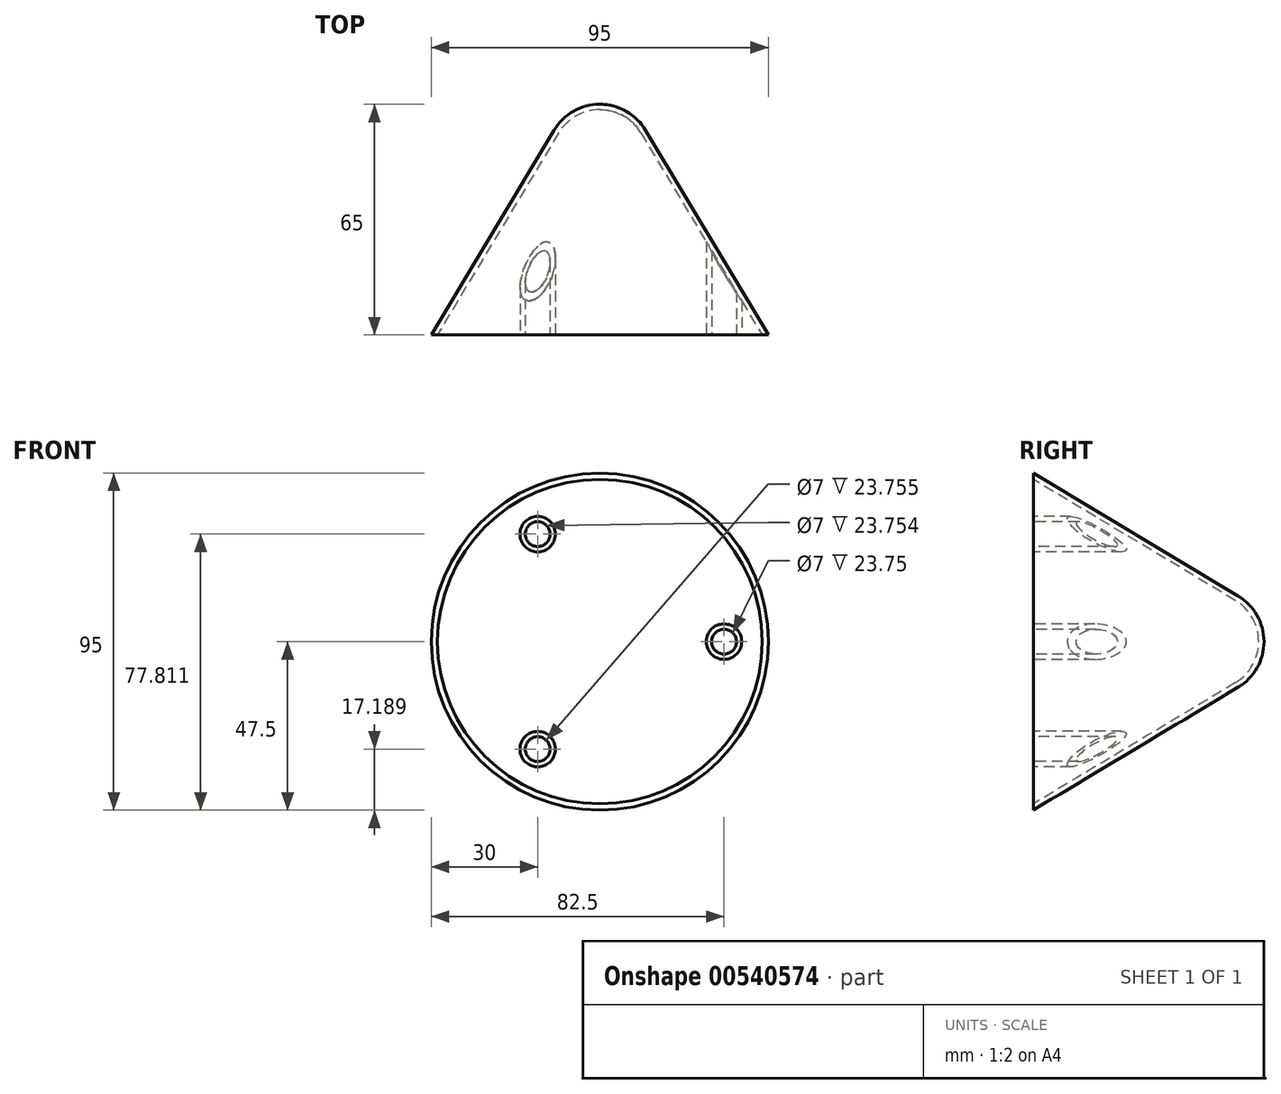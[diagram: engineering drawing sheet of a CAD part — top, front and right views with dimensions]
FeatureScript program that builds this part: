
annotation { "Feature Type Name" : "Feature", "Feature Type Description" : "" }
export const myFeature = defineFeature(function(context is Context, id is Id, definition is map)
    precondition{}
    {
        {
            var Q0;
            Q0=qCreatedBy(makeId("Top.planeOp"),FACE);
            var sketch = newSketch(context, id + "F0", { "sketchPlane" : qUnion([Q0])});
            skLineSegment(sketch, "E0", {"start": v(0, 0) * mm, "end": v(47.5, 0) * mm});
            skLineSegment(sketch, "E1", {"start": v(0, 0) * mm, "end": v(0, 50) * mm});
            skArc(sketch, "E2", {"start": v(12.86, 57.72) * mm, "mid": v(7.39, 63.05) * mm, "end": v(0, 65) * mm});
            skLineSegment(sketch, "E3", {"start": v(12.86, 57.72) * mm, "end": v(47.5, 0) * mm});
            skLineSegment(sketch, "E4", {"start": v(0, 50) * mm, "end": v(0, 77.84) * mm});
            skPoint(sketch, "E5.orphan", {"position": v(-12.86, 57.72) * mm});
            skSolve(sketch);
        }
        {
            var Q0;
            Q0=makeQuery(id+"F0.imprint","IMPRINT",FACE,{"disambiguationData":[TD([[makeQuery(id+"F0.imprint","IMPRINT",EDGE,{"derivedFrom":sQuery(id+"F0.wireOp",EDGE,"E0")}),1.0]])]});
            var Q1;
            Q1=sQuery(id+"F0.wireOp",EDGE,"E1");
            revolve(context, id + "F1", {"entities" : qUnion([Q0]), "axis" : qUnion([Q1]), "revolveType" : RevolveType.FULL});
        }
        {
            var Q0;
            Q0=makeQuery(id+"F1.opRevolve","SWEPT_FACE",FACE,{"disambiguationData":[OSD([sQuery(id+"F0.wireOp",EDGE,"E0")])]});
            shell(context, id + "F2", {"entities" : qUnion([Q0]), "thickness" : 1.5 * mm});
        }
        {
            var Q0;
            Q0=qCreatedBy(makeId("Front.planeOp"),FACE);
            var sketch = newSketch(context, id + "F3", { "sketchPlane" : qUnion([Q0])});
            skCircle(sketch, "E6", {"center": v(35, 0) * mm, "radius": 5 * mm});
            skCircle(sketch, "E7.1.0", {"center": v(-17.5, 30.31) * mm, "radius": 5 * mm});
            skCircle(sketch, "E7.2.0", {"center": v(-17.5, -30.31) * mm, "radius": 5 * mm});
            skPoint(sketch, "E7.center", {"position": v(0, 0) * mm});
            skSolve(sketch);
        }
        {
            var Q0;
            Q0 = qSketchRegion(id + "F3", true);
            extrude(context, id + "F4", {"entities" : qUnion([Q0]), "operationType" : NewBodyOperationType.ADD, "endBound" : BoundingType.UP_TO_NEXT, "oppositeDirection" : true, "depth" : 25 * mm, "offsetDistance" : 25 * mm});
        }
        {
            var Q0;
            Q0=makeQuery(id+"F4.opExtrude","CAP_FACE",FACE,{"disambiguationData":[OSD([sQuery(id+"F3.wireOp",EDGE,"E7.1.0")])],"isStart":true});
            var Q1;
            Q1=makeQuery(id+"F4.opExtrude","CAP_FACE",FACE,{"disambiguationData":[OSD([sQuery(id+"F3.wireOp",EDGE,"E6")])],"isStart":true});
            var Q2;
            Q2=makeQuery(id+"F4.opExtrude","CAP_FACE",FACE,{"disambiguationData":[OSD([sQuery(id+"F3.wireOp",EDGE,"E7.2.0")])],"isStart":true});
            shell(context, id + "F5", {"entities" : qUnion([Q0, Q1, Q2]), "thickness" : 1.5 * mm});
        }
    });
